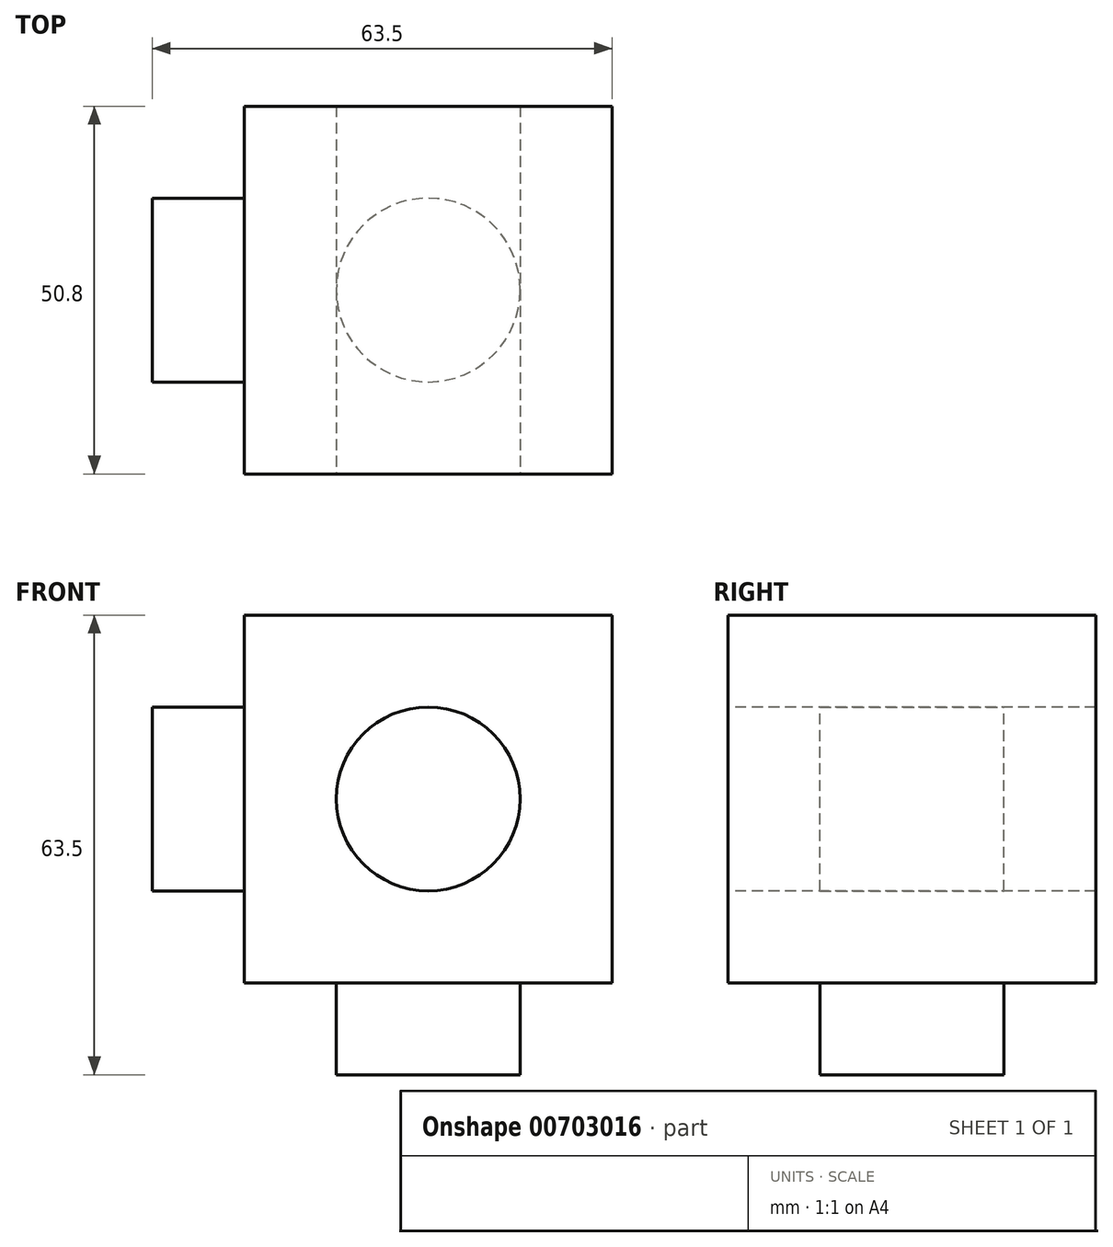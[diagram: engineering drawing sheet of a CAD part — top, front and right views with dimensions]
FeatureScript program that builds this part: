
annotation { "Feature Type Name" : "Feature", "Feature Type Description" : "" }
export const myFeature = defineFeature(function(context is Context, id is Id, definition is map)
    precondition{}
    {
        {
            var Q0;
            Q0=qCreatedBy(makeId("Front.planeOp"),FACE);
            var sketch = newSketch(context, id + "F0", { "sketchPlane" : qUnion([Q0])});
            skLineSegment(sketch, "E0.bottom", {"start": v(0, 0) * mm, "end": v(50.8, 0) * mm});
            skLineSegment(sketch, "E0.top", {"start": v(0, 50.8) * mm, "end": v(50.8, 50.8) * mm});
            skLineSegment(sketch, "E0.left", {"start": v(0, 0) * mm, "end": v(0, 50.8) * mm});
            skLineSegment(sketch, "E0.right", {"start": v(50.8, 0) * mm, "end": v(50.8, 50.8) * mm});
            skSolve(sketch);
        }
        {
            var Q0;
            Q0 = qSketchRegion(id + "F0", true);
            extrude(context, id + "F1", {"entities" : qUnion([Q0]), "depth" : 50.8 * mm, "offsetDistance" : 25.4 * mm});
        }
        {
            var Q0;
            Q0=makeQuery(id+"F1.opExtrude","CAP_FACE",FACE,{"disambiguationData":[OSD([sQuery(id+"F0.wireOp",EDGE,"E0.bottom"),sQuery(id+"F0.wireOp",EDGE,"E0.top"),sQuery(id+"F0.wireOp",EDGE,"E0.left"),sQuery(id+"F0.wireOp",EDGE,"E0.right")])],"isStart":false});
            var sketch = newSketch(context, id + "F2", { "sketchPlane" : qUnion([Q0])});
            skCircle(sketch, "E1", {"center": v(25.4, 25.4) * mm, "radius": 12.7 * mm});
            skSolve(sketch);
        }
        {
            var Q0;
            Q0=makeQuery(id+"F2.imprint","IMPRINT",FACE,{"disambiguationData":[TD([[makeQuery(id+"F2.imprint","IMPRINT",EDGE,{"derivedFrom":sQuery(id+"F2.wireOp",EDGE,"E1")}),1.0]])]});
            extrude(context, id + "F3", {"entities" : qUnion([Q0]), "operationType" : NewBodyOperationType.REMOVE, "oppositeDirection" : true, "depth" : 558.8 * mm, "offsetDistance" : 25.4 * mm});
        }
        {
            var Q0;
            Q0=makeQuery(id+"F1.opExtrude","SWEPT_FACE",FACE,{"disambiguationData":[OSD([sQuery(id+"F0.wireOp",EDGE,"E0.bottom")])]});
            var sketch = newSketch(context, id + "F4", { "sketchPlane" : qUnion([Q0])});
            skCircle(sketch, "E2", {"center": v(25.4, 25.4) * mm, "radius": 12.7 * mm});
            skSolve(sketch);
        }
        {
            var Q0;
            Q0 = qSketchRegion(id + "F4", true);
            extrude(context, id + "F5", {"entities" : qUnion([Q0]), "operationType" : NewBodyOperationType.ADD, "depth" : 12.7 * mm, "offsetDistance" : 25.4 * mm});
        }
        {
            var Q0;
            Q0=makeQuery(id+"F1.opExtrude","SWEPT_FACE",FACE,{"disambiguationData":[OSD([sQuery(id+"F0.wireOp",EDGE,"E0.left")])]});
            var sketch = newSketch(context, id + "F6", { "sketchPlane" : qUnion([Q0])});
            skLineSegment(sketch, "E3.bottom", {"start": v(38.1, 12.7) * mm, "end": v(12.7, 12.7) * mm});
            skLineSegment(sketch, "E3.top", {"start": v(38.1, 38.1) * mm, "end": v(12.7, 38.1) * mm});
            skLineSegment(sketch, "E3.left", {"start": v(38.1, 12.7) * mm, "end": v(38.1, 38.1) * mm});
            skLineSegment(sketch, "E3.right", {"start": v(12.7, 12.7) * mm, "end": v(12.7, 38.1) * mm});
            skSolve(sketch);
        }
        {
            var Q0;
            Q0=makeQuery(id+"F6.imprint","IMPRINT",FACE,{"disambiguationData":[TD([[makeQuery(id+"F6.imprint","IMPRINT",EDGE,{"derivedFrom":sQuery(id+"F6.wireOp",EDGE,"E3.bottom")}),-1.0]])]});
            extrude(context, id + "F7", {"entities" : qUnion([Q0]), "operationType" : NewBodyOperationType.ADD, "depth" : 12.7 * mm, "offsetDistance" : 25.4 * mm});
        }
    });
